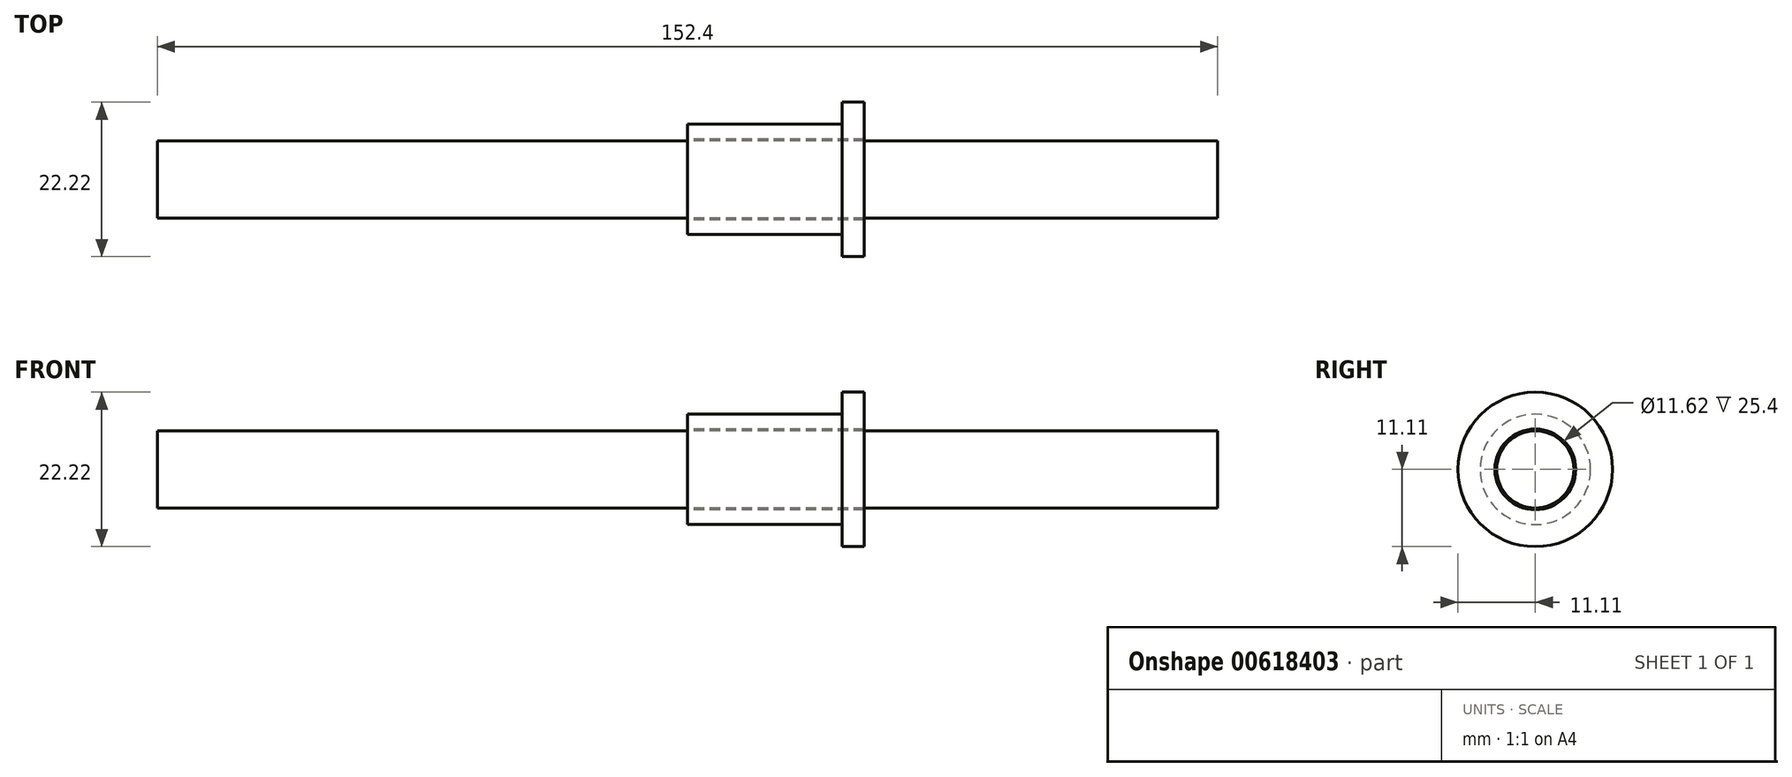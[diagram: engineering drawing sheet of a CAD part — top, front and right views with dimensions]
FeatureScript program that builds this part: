
annotation { "Feature Type Name" : "Feature", "Feature Type Description" : "" }
export const myFeature = defineFeature(function(context is Context, id is Id, definition is map)
    precondition{}
    {
        {
            var Q0;
            Q0=qCreatedBy(makeId("Right.planeOp"),FACE);
            var sketch = newSketch(context, id + "F0", { "sketchPlane" : qUnion([Q0])});
            skCircle(sketch, "E0", {"center": v(0, 0) * mm, "radius": 7.94 * mm});
            skCircle(sketch, "E1", {"center": v(0, 0) * mm, "radius": 5.56 * mm});
            skCircle(sketch, "E2.0", {"center": v(0, 0) * mm, "radius": 5.81 * mm});
            skSolve(sketch);
        }
        {
            var Q0;
            Q0=makeQuery(id+"F0.imprint","IMPRINT",FACE,{"disambiguationData":[TD([[makeQuery(id+"F0.imprint","IMPRINT",EDGE,{"derivedFrom":sQuery(id+"F0.wireOp",EDGE,"E1")}),1.0]])]});
            extrude(context, id + "F1", {"entities" : qUnion([Q0]), "endBound" : BoundingType.SYMMETRIC, "depth" : 152.4 * mm, "offsetDistance" : 25.4 * mm});
        }
        {
            var Q0;
            Q0=makeQuery(id+"F0.imprint","IMPRINT",FACE,{"disambiguationData":[TD([[makeQuery(id+"F0.imprint","IMPRINT",EDGE,{"derivedFrom":sQuery(id+"F0.wireOp",EDGE,"E0")}),1.0]])]});
            extrude(context, id + "F2", {"entities" : qUnion([Q0]), "depth" : 25.4 * mm, "offsetDistance" : 25.4 * mm});
        }
        {
            var Q0;
            Q0=makeQuery(id+"F2.opExtrude","CAP_FACE",FACE,{"disambiguationData":[OSD([sQuery(id+"F0.wireOp",EDGE,"E0"),sQuery(id+"F0.wireOp",EDGE,"E2.0")])],"isStart":false});
            var sketch = newSketch(context, id + "F3", { "sketchPlane" : qUnion([Q0])});
            skCircle(sketch, "E3.0", {"center": v(0, 0) * mm, "radius": 11.11 * mm});
            skSolve(sketch);
        }
        {
            var Q0;
            Q0=makeQuery(id+"F3.imprint","IMPRINT",FACE,{"disambiguationData":[TD([[makeQuery(id+"F3.imprint","IMPRINT",EDGE,{"derivedFrom":sQuery(id+"F3.wireOp",EDGE,"E3.0")}),1.0]])]});
            extrude(context, id + "F4", {"entities" : qUnion([Q0]), "operationType" : NewBodyOperationType.ADD, "depth" : -3.17 * mm, "offsetDistance" : 25.4 * mm});
        }
    });
